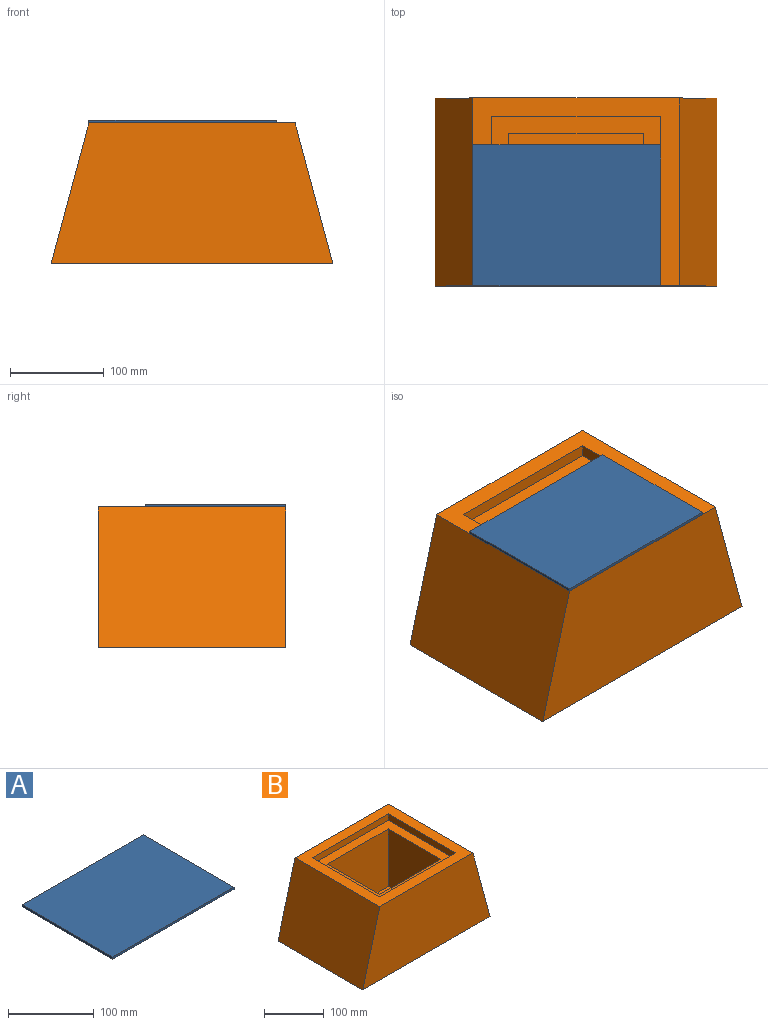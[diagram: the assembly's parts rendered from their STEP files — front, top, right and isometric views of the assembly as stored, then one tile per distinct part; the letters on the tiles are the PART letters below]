
ASSEMBLY  parts=2 mates=1
PART A: 6 faces, bbox 200x150x3 mm
  f0: plane 200x3mm, normal (0,1,0), area 600mm2, adj f1,f3,f4,f5
  f1: plane 150x3mm, normal (-1,0,0), area 450mm2, adj f0,f2,f4,f5
  f2: plane 200x3mm, normal (0,-1,0), area 600mm2, adj f1,f3,f4,f5
  f3: plane 150x3mm, normal (1,0,0), area 450mm2, adj f0,f2,f4,f5
  f4: plane 200x150mm, normal (0,0,1), area 30000mm2, adj f0,f1,f2,f3
  f5: plane 200x150mm, normal (0,0,-1), area 30000mm2, adj f0,f1,f2,f3
PART B: 16 faces, bbox 300x200x150 mm
  f0: plane 200x150mm, normal (-0.97,0,0.26), area 31058.3mm2, adj f1,f3,f4,f5
  f1: plane 300x200mm, normal (0,0,-1), area 60000mm2, adj f0,f2,f4,f5
  f2: plane 200x150mm, normal (0.97,0,0.26), area 31058.3mm2, adj f1,f3,f4,f5
  f3: plane 219.62x200mm, normal (0,0,1), area 15184.6mm2, adj f0,f2,f4,f5,f6,f7,f8,f9
  f4: plane 300x150mm, normal (0,-1,0), area 38971.1mm2, adj f0,f1,f2,f3
  f5: plane 300x150mm, normal (0,1,0), area 38971.1mm2, adj f0,f1,f2,f3
  f6: plane 179.62x13mm, normal (0,-1,0), area 2335mm2, adj f3,f7,f9,f10
  f7: plane 160x13mm, normal (1,0,0), area 2080mm2, adj f3,f6,f8,f10
  f8: plane 179.62x13mm, normal (0,1,0), area 2335mm2, adj f3,f7,f9,f10
  f9: plane 160x13mm, normal (-1,0,0), area 2080mm2, adj f3,f6,f8,f10
  f10: plane 179.62x160mm, normal (0,0,1), area 10930.1mm2, adj f6,f7,f8,f9,f12,f13,f14,f15
  f11: plane 143.62x124mm, normal (0,0,1), area 17808.3mm2, adj f12,f13,f14,f15
  f12: plane 143.62x117mm, normal (0,1,0), area 16803mm2, adj f10,f11,f13,f15
  f13: plane 124x117mm, normal (1,0,0), area 14508mm2, adj f10,f11,f12,f14
  f14: plane 143.62x117mm, normal (0,-1,0), area 16803mm2, adj f10,f11,f13,f15
  f15: plane 124x117mm, normal (-1,0,0), area 14508mm2, adj f10,f11,f12,f14
PLACE A t=(-55.75,-19.67,20.93)mm
PLACE B t=(-55.18,84.08,-51.95)mm
MATE fastened B.f3 <-> A.f5  axis (0,0,1) through (-163.47,-115.92,20.93)mm
